# Revit family: Grab_Bar-TSL-GR45600-THESPLASHLAB
name_source: partatom
category: Specialty Equipment
revit_build: Autodesk Revit 2016 (Build: 20160314_0715(x64)
units: mm (PartAtom-declared; Revit-internal decimal feet)

## family parameters
Cut with Voids When Loaded = No
Host = Face
OmniClass Number = 23.40.20.21.47
OmniClass Title = Bath Grab Bars
Part Type = Normal
Room Calculation Point = No
Round Connector Dimension = Use Diameter
Shared = No

## types (5) — shared parameters
Assembly Code = C1030200
AssetType = fixed
Default Elevation = 900 mm  [stored 2.95276 ft]
DocumentationInstallationGuide = www.thesplashlab.com
DocumentationLiterature = www.thesplashlab.com
DocumentationMaintenance = www.thesplashlab.com
DocumentationTechnical = www.thesplashlab.com
DurationUnit = years
ExpectedLife = 2
Grade = 304
Keynote = N13/340
Manufacturer = The Splash Lab
Manufacturer Tel = 0161 482 7000
Material = Stainless Steel
Model = TSL-GR45600
Mtrl_Grade = 304
Mtrl_Material = Stainless Steel
NBSObjectName = Grab_Bar-TSL-GR45600-THESPLASHLAB
NBSReference = 45-35-72/368
Product Documentation Link = www.thesplashlab.com
Product O&M Link = www.thesplashlab.com
Product Page Link = www.thesplashlab.com
Product Specification Link = www.thesplashlab.com
TypeName = TSL-GR45600
URL = www.thesplashlab.com
Uniclass2 = 45-35-72/368
WarrantyDescription = 2 years from date of purchase
WarrantyDurationParts = 24
WarrantyDurationUnit = months
_current revision = 1
_distributed by = www.thesplashlab.com
material test = <By Category>
zero-valued in all types: Mtrl_ExpectedLife, Mtrl_ReplacementCost, Mtrl_SerialNumber, Mtrl_TagNumber, Mtrl_WarrantyDurationLabor, Mtrl_WarrantyDurationParts, Mtrl_bimspec_guid, Mtrl_current revision, _BIMspec_GUID

## per-type parameters (varying)
| type | Description | Finish | Mtrl_Finish | Type Comments | finish |
| TSL-GR45600_Steel | The GR-45-600 is a 600mm straight grab bar, which comes with concealed fixing roses. | Brushed Stainless Steel | Brushed Stainless Steel | Brushed Stainless Steel | Brushed Stainless Steel |
| TSL-GR45600_Copper | The GR-45-600 is a 600mm straight grab bar, which comes with concealed fixing roses. | Brushed Copper | Brushed Copper | Brushed Copper | Brushed Copper |
| TSL-GR45600_Brass | The GR-45-600 is a 600mm straight grab bar, which comes with concealed fixing roses. | Brushed Brass | Brushed Brass | Brushed Brass | Brushed Brass |
| TSL-GR45600_Bronze | The GR-45-600 is a 600mm straight grab bar, which comes with concealed fixing roses. | Brushed Bronze | Brushed Bronze | Brushed Bronze | Brushed Bronze |
| TSL-GR45600_Black | The TSL-GR45600 is a 600mm straight grab bar, which comes with concealed fixing roses. | Brushed Black | Brushed Black | Brushed Black | Brushed Black |

note: [stored X ft] marks values corroborated as IEEE doubles in the binary element streams (Revit-internal decimal feet)

## geometry (parser evidence)
native form markers: Blend x2, Sweep x2
no freeform markers — native parametric forms only
